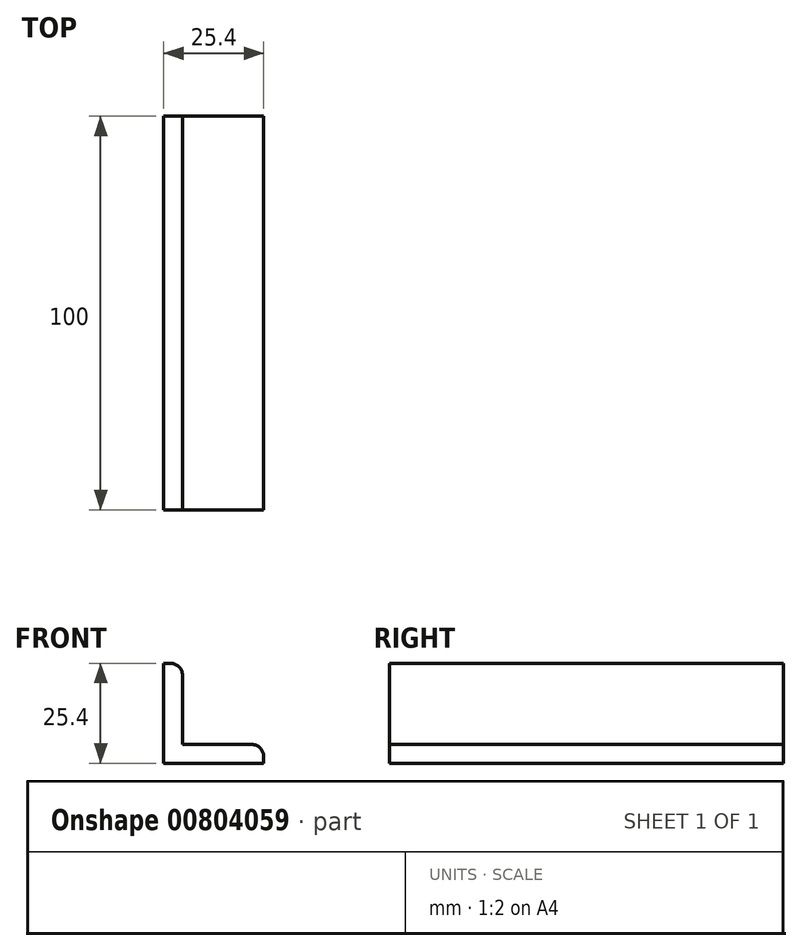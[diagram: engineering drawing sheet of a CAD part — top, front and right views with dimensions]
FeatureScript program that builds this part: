
annotation { "Feature Type Name" : "Feature", "Feature Type Description" : "" }
export const myFeature = defineFeature(function(context is Context, id is Id, definition is map)
    precondition{}
    {
        {
            var Q0;
            Q0=qCreatedBy(makeId("Front.planeOp"),FACE);
            var sketch = newSketch(context, id + "F0", { "sketchPlane" : qUnion([Q0])});
            skLineSegment(sketch, "E0", {"start": v(0, 0) * mm, "end": v(0, 25.4) * mm});
            skLineSegment(sketch, "E1", {"start": v(0, 0) * mm, "end": v(25.4, 0) * mm});
            skLineSegment(sketch, "E2", {"start": v(0, 25.4) * mm, "end": v(1.76, 25.4) * mm});
            skLineSegment(sketch, "E3", {"start": v(25.4, 0) * mm, "end": v(25.4, 1.76) * mm});
            skLineSegment(sketch, "E4", {"start": v(22.4, 4.76) * mm, "end": v(4.76, 4.76) * mm});
            skLineSegment(sketch, "E5", {"start": v(4.76, 4.76) * mm, "end": v(4.76, 22.4) * mm});
            skPoint(sketch, "E6.visualSharp", {"position": v(25.4, 4.76) * mm});
            skArc(sketch, "E6.filletArc", {"start": v(25.4, 1.76) * mm, "mid": v(24.52, 3.88) * mm, "end": v(22.4, 4.76) * mm});
            skPoint(sketch, "E7.visualSharp", {"position": v(4.76, 25.4) * mm});
            skArc(sketch, "E7.filletArc", {"start": v(4.76, 22.4) * mm, "mid": v(3.88, 24.52) * mm, "end": v(1.76, 25.4) * mm});
            skSolve(sketch);
        }
        {
            var Q0;
            Q0=makeQuery(id+"F0.imprint","IMPRINT",FACE,{"disambiguationData":[TD([[makeQuery(id+"F0.imprint","IMPRINT",EDGE,{"derivedFrom":sQuery(id+"F0.wireOp",EDGE,"E0")}),-1.0]])]});
            extrude(context, id + "F1", {"entities" : qUnion([Q0]), "depth" : 100 * mm, "offsetDistance" : 25 * mm});
        }
    });
